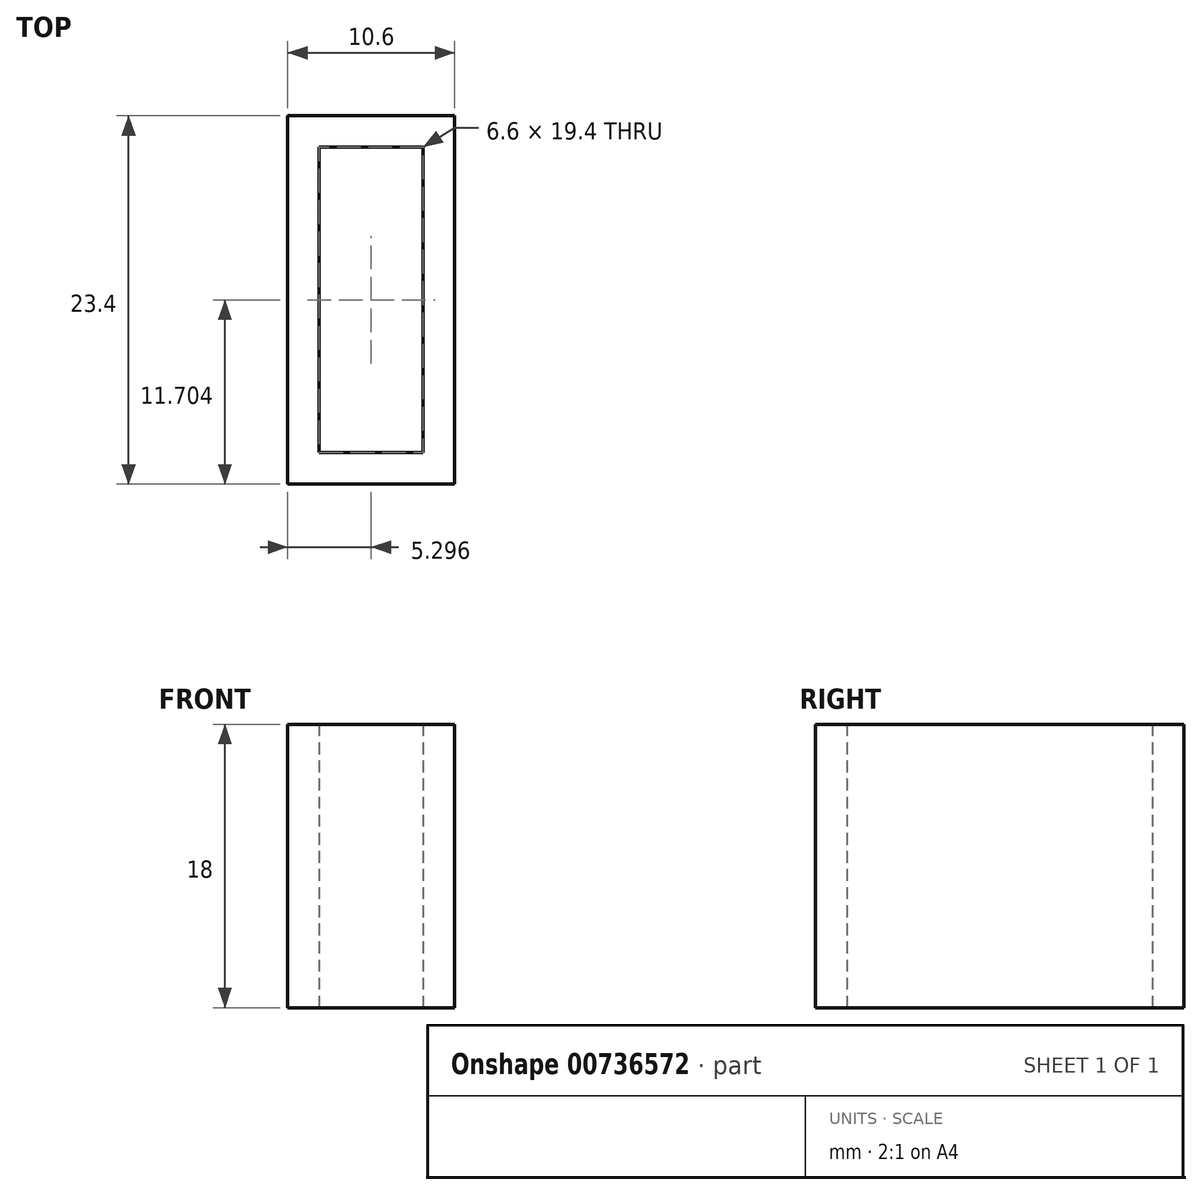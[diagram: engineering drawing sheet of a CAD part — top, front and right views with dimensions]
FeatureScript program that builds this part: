
annotation { "Feature Type Name" : "Feature", "Feature Type Description" : "" }
export const myFeature = defineFeature(function(context is Context, id is Id, definition is map)
    precondition{}
    {
        {
            var Q0;
            Q0=qCreatedBy(makeId("Top.planeOp"),FACE);
            var sketch = newSketch(context, id + "F0", { "sketchPlane" : qUnion([Q0])});
            skLineSegment(sketch, "E0.bottom", {"start": v(3.3, -12.94) * mm, "end": v(9.9, -12.94) * mm});
            skLineSegment(sketch, "E0.top", {"start": v(3.3, -32.34) * mm, "end": v(9.9, -32.34) * mm});
            skLineSegment(sketch, "E0.left", {"start": v(3.3, -12.94) * mm, "end": v(3.3, -32.34) * mm});
            skLineSegment(sketch, "E0.right", {"start": v(9.9, -12.94) * mm, "end": v(9.9, -32.34) * mm});
            skLineSegment(sketch, "E1.bottom", {"start": v(1.3, -10.94) * mm, "end": v(11.9, -10.94) * mm});
            skLineSegment(sketch, "E1.top", {"start": v(1.3, -34.34) * mm, "end": v(11.9, -34.34) * mm});
            skLineSegment(sketch, "E1.left", {"start": v(1.3, -10.94) * mm, "end": v(1.3, -34.34) * mm});
            skLineSegment(sketch, "E1.right", {"start": v(11.9, -10.94) * mm, "end": v(11.9, -34.34) * mm});
            skSolve(sketch);
        }
        {
            var Q0;
            Q0=makeQuery(id+"F0.imprint","IMPRINT",FACE,{"disambiguationData":[TD([[makeQuery(id+"F0.imprint","IMPRINT",EDGE,{"derivedFrom":sQuery(id+"F0.wireOp",EDGE,"E0.bottom")}),1.0]])]});
            extrude(context, id + "F1", {"entities" : qUnion([Q0]), "depth" : 18 * mm, "offsetDistance" : 25 * mm});
        }
    });
